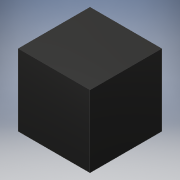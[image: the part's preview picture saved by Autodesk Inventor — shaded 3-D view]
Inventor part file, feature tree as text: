
AUTODESK INVENTOR PART (.ipt)
format: ipt  version: 2019 (Build 230136000, 136)  size: 88,064 bytes
history: native  units: mm
features: extrude x1, sketch x1
ambient origin geometry x8: Origin, YZ Plane, XZ Plane, XY Plane, X Axis, Y Axis, Z Axis, Center Point
bodies: Solid1 (feature_tree)
feature tree (2):
  extrude  "Extrusion1"  Depth=10.0mm
  sketch  "Sketch1"  dims[d0=10.0mm d1=10.0mm d2=10.0mm d3=0.0mm]
